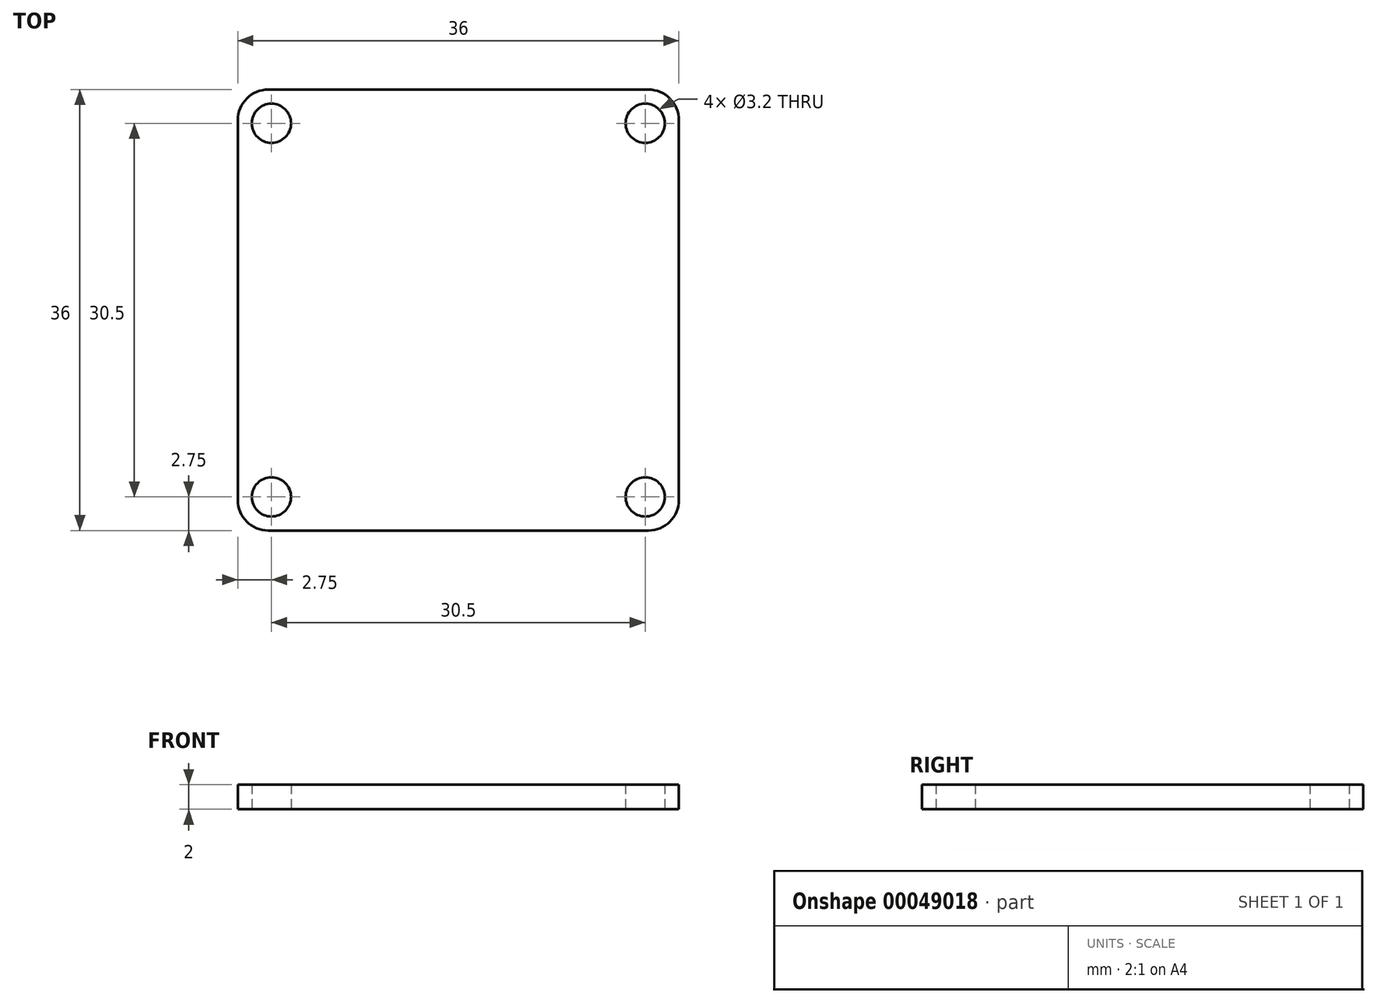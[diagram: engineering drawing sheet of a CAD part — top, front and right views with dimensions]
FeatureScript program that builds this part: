
annotation { "Feature Type Name" : "Feature", "Feature Type Description" : "" }
export const myFeature = defineFeature(function(context is Context, id is Id, definition is map)
    precondition{}
    {
        {
            var Q0;
            Q0=qCreatedBy(makeId("Top.planeOp"),FACE);
            var sketch = newSketch(context, id + "F0", { "sketchPlane" : qUnion([Q0])});
            skLineSegment(sketch, "E0.bottom", {"start": v(15.5, 18) * mm, "end": v(-15.5, 18) * mm});
            skLineSegment(sketch, "E0.top", {"start": v(15.5, -18) * mm, "end": v(-15.5, -18) * mm});
            skLineSegment(sketch, "E0.left", {"start": v(18, 15.5) * mm, "end": v(18, -15.5) * mm});
            skLineSegment(sketch, "E0.right", {"start": v(-18, 15.5) * mm, "end": v(-18, -15.5) * mm});
            skPoint(sketch, "E0.middle", {"position": v(0, 0) * mm});
            skPoint(sketch, "E1.visualSharp", {"position": v(-18, 18) * mm});
            skArc(sketch, "E1.filletArc", {"start": v(-15.5, 18) * mm, "mid": v(-17.27, 17.27) * mm, "end": v(-18, 15.5) * mm});
            skPoint(sketch, "E2.visualSharp", {"position": v(18, 18) * mm});
            skArc(sketch, "E2.filletArc", {"start": v(18, 15.5) * mm, "mid": v(17.27, 17.27) * mm, "end": v(15.5, 18) * mm});
            skPoint(sketch, "E3.visualSharp", {"position": v(18, -18) * mm});
            skArc(sketch, "E3.filletArc", {"start": v(15.5, -18) * mm, "mid": v(17.27, -17.27) * mm, "end": v(18, -15.5) * mm});
            skPoint(sketch, "E4.visualSharp", {"position": v(-18, -18) * mm});
            skArc(sketch, "E4.filletArc", {"start": v(-18, -15.5) * mm, "mid": v(-17.27, -17.27) * mm, "end": v(-15.5, -18) * mm});
            skLineSegment(sketch, "E5", {"start": v(0, 0) * mm, "end": v(18, 18) * mm, "construction": true});
            skLineSegment(sketch, "E6", {"start": v(0, 0) * mm, "end": v(-18, 18) * mm, "construction": true});
            skCircle(sketch, "E7", {"center": v(15.25, 15.25) * mm, "radius": 1.6 * mm});
            skCircle(sketch, "E8.1.0", {"center": v(15.25, -15.25) * mm, "radius": 1.6 * mm});
            skCircle(sketch, "E8.2.0", {"center": v(-15.25, -15.25) * mm, "radius": 1.6 * mm});
            skCircle(sketch, "E8.3.0", {"center": v(-15.25, 15.25) * mm, "radius": 1.6 * mm});
            skLineSegment(sketch, "E8.anchor1", {"start": v(0, 0) * mm, "end": v(15.25, 15.25) * mm, "construction": true});
            skLineSegment(sketch, "E8.anchor2", {"start": v(0, 0) * mm, "end": v(-15.25, 15.25) * mm, "construction": true});
            skSolve(sketch);
        }
        {
            var Q0;
            Q0 = qSketchRegion(id + "F0", true);
            extrude(context, id + "F1", {"entities" : qUnion([Q0]), "depth" : 2 * mm});
        }
    });
